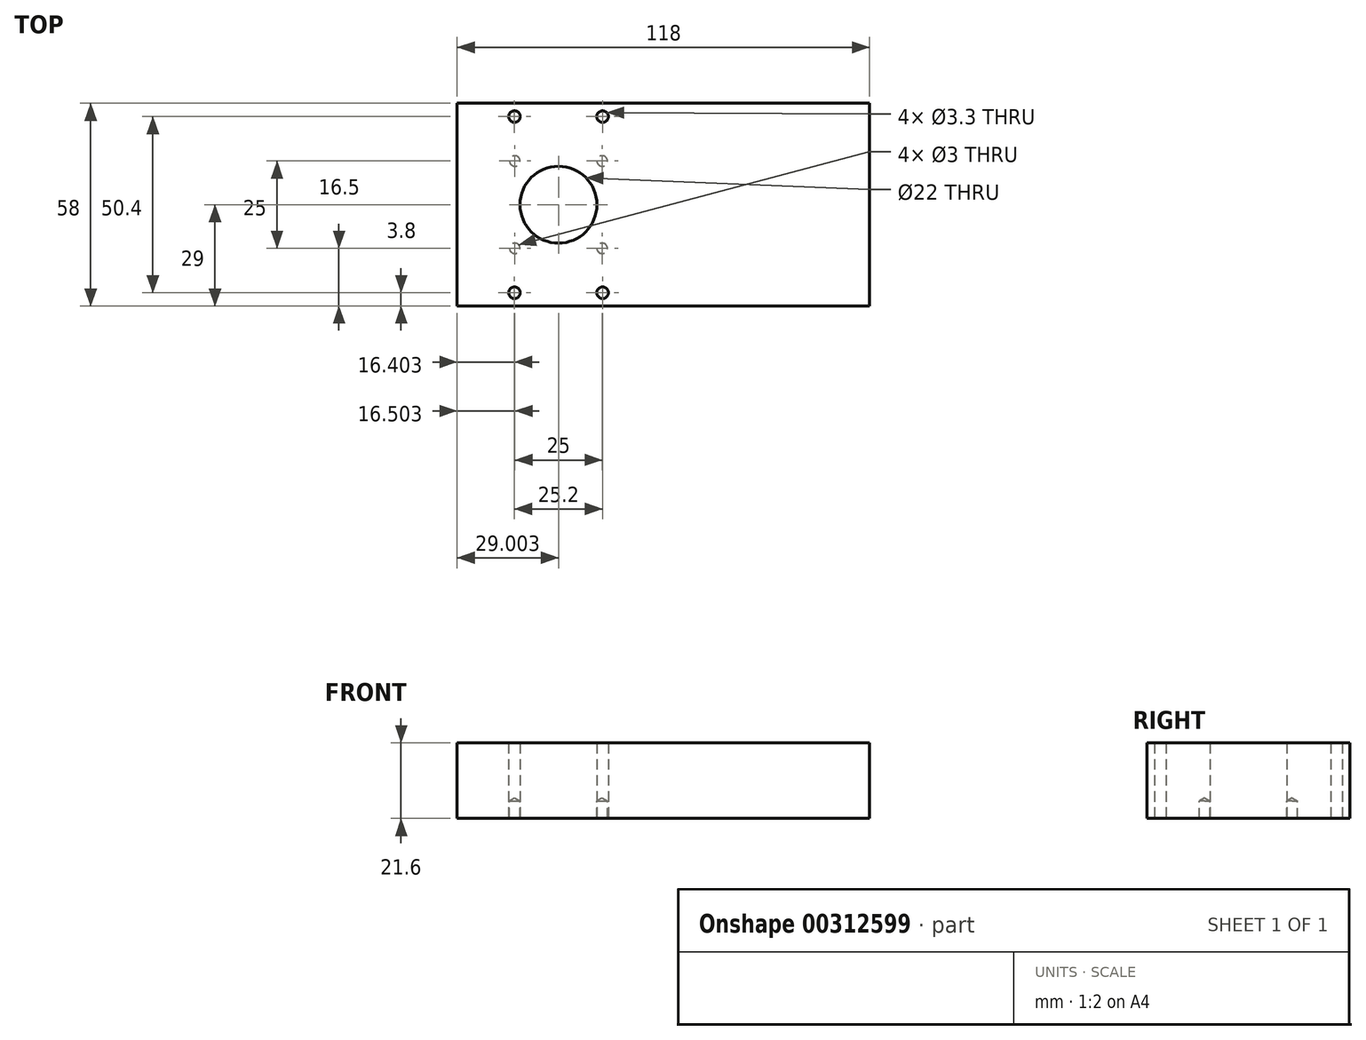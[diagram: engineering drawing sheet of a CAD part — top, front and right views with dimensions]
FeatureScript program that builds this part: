
annotation { "Feature Type Name" : "Feature", "Feature Type Description" : "" }
export const myFeature = defineFeature(function(context is Context, id is Id, definition is map)
    precondition{}
    {
        {
            var Q0;
            Q0=qCreatedBy(makeId("Top.planeOp"),FACE);
            var sketch = newSketch(context, id + "F0", { "sketchPlane" : qUnion([Q0])});
            skLineSegment(sketch, "E0.bottom", {"start": v(-54.05, 21.91) * mm, "end": v(63.95, 21.91) * mm});
            skLineSegment(sketch, "E0.top", {"start": v(-54.05, -36.09) * mm, "end": v(63.95, -36.09) * mm});
            skLineSegment(sketch, "E0.left", {"start": v(-54.05, 21.91) * mm, "end": v(-54.05, -36.09) * mm});
            skLineSegment(sketch, "E0.right", {"start": v(63.95, 21.91) * mm, "end": v(63.95, -36.09) * mm});
            skCircle(sketch, "E1", {"center": v(-37.65, 18.11) * mm, "radius": 1.65 * mm});
            skCircle(sketch, "E2", {"center": v(-12.45, 18.11) * mm, "radius": 1.65 * mm});
            skLineSegment(sketch, "E3", {"start": v(-54.05, -7.09) * mm, "end": v(63.95, -7.09) * mm, "construction": true});
            skLineSegment(sketch, "E4", {"start": v(4.95, 21.91) * mm, "end": v(4.95, -36.09) * mm, "construction": true});
            skCircle(sketch, "E5.MirrorC", {"center": v(-12.45, -32.29) * mm, "radius": 1.65 * mm});
            skCircle(sketch, "E6.MirrorC", {"center": v(-37.65, -32.29) * mm, "radius": 1.65 * mm});
            skCircle(sketch, "E7", {"center": v(-25.05, -7.09) * mm, "radius": 11 * mm});
            skLineSegment(sketch, "E8", {"start": v(-37.65, 18.11) * mm, "end": v(-12.45, -32.29) * mm, "construction": true});
            skLineSegment(sketch, "E9", {"start": v(-37.55, 5.41) * mm, "end": v(-12.55, -19.59) * mm, "construction": true});
            skLineSegment(sketch, "E10", {"start": v(-12.55, 5.41) * mm, "end": v(-37.55, -19.59) * mm, "construction": true});
            skPoint(sketch, "E11", {"position": v(-37.55, -19.59) * mm});
            skPoint(sketch, "E12", {"position": v(-12.55, -19.59) * mm});
            skPoint(sketch, "E13", {"position": v(-12.55, 5.41) * mm});
            skPoint(sketch, "E14", {"position": v(-37.55, 5.41) * mm});
            skSolve(sketch);
        }
        {
            var Q0;
            Q0=makeQuery(id+"F0.imprint","IMPRINT",FACE,{"disambiguationData":[TD([[makeQuery(id+"F0.imprint","IMPRINT",EDGE,{"derivedFrom":sQuery(id+"F0.wireOp",EDGE,"E0.bottom")}),-1.0]])]});
            extrude(context, id + "F1", {"entities" : qUnion([Q0]), "depth" : 21.6 * mm});
        }
        {
            var Q0;
            Q0=sQuery(id+"F0.wireOp",VERTEX,"E11");
            var Q1;
            Q1=sQuery(id+"F0.wireOp",VERTEX,"E12");
            var Q2;
            Q2=sQuery(id+"F0.wireOp",VERTEX,"E13");
            var Q3;
            Q3=sQuery(id+"F0.wireOp",VERTEX,"E14");
            var Q4;
            Q4=makeQuery(id+"F1.opExtrude","SWEPT_BODY",BODY,{"disambiguationData":[OSD([sQuery(id+"F0.wireOp",EDGE,"E0.bottom"),sQuery(id+"F0.wireOp",EDGE,"E0.top"),sQuery(id+"F0.wireOp",EDGE,"E0.left"),sQuery(id+"F0.wireOp",EDGE,"E0.right"),sQuery(id+"F0.wireOp",EDGE,"E1"),sQuery(id+"F0.wireOp",EDGE,"E2"),sQuery(id+"F0.wireOp",EDGE,"E5.MirrorC"),sQuery(id+"F0.wireOp",EDGE,"E6.MirrorC"),sQuery(id+"F0.wireOp",EDGE,"E7")])]});
            hole(context, id + "F2", {"style" : HoleStyle.SIMPLE, "endStyle" : HoleEndStyle.BLIND, "oppositeDirection" : true, "holeDiameter" : 3 * mm, "holeDepth" : 5 * mm, "tappedDepth" : 12 * mm, "tapClearance" : 3, "locations" : qUnion([Q0, Q1, Q2, Q3]), "scope" : qUnion([Q4])});
        }
    });
